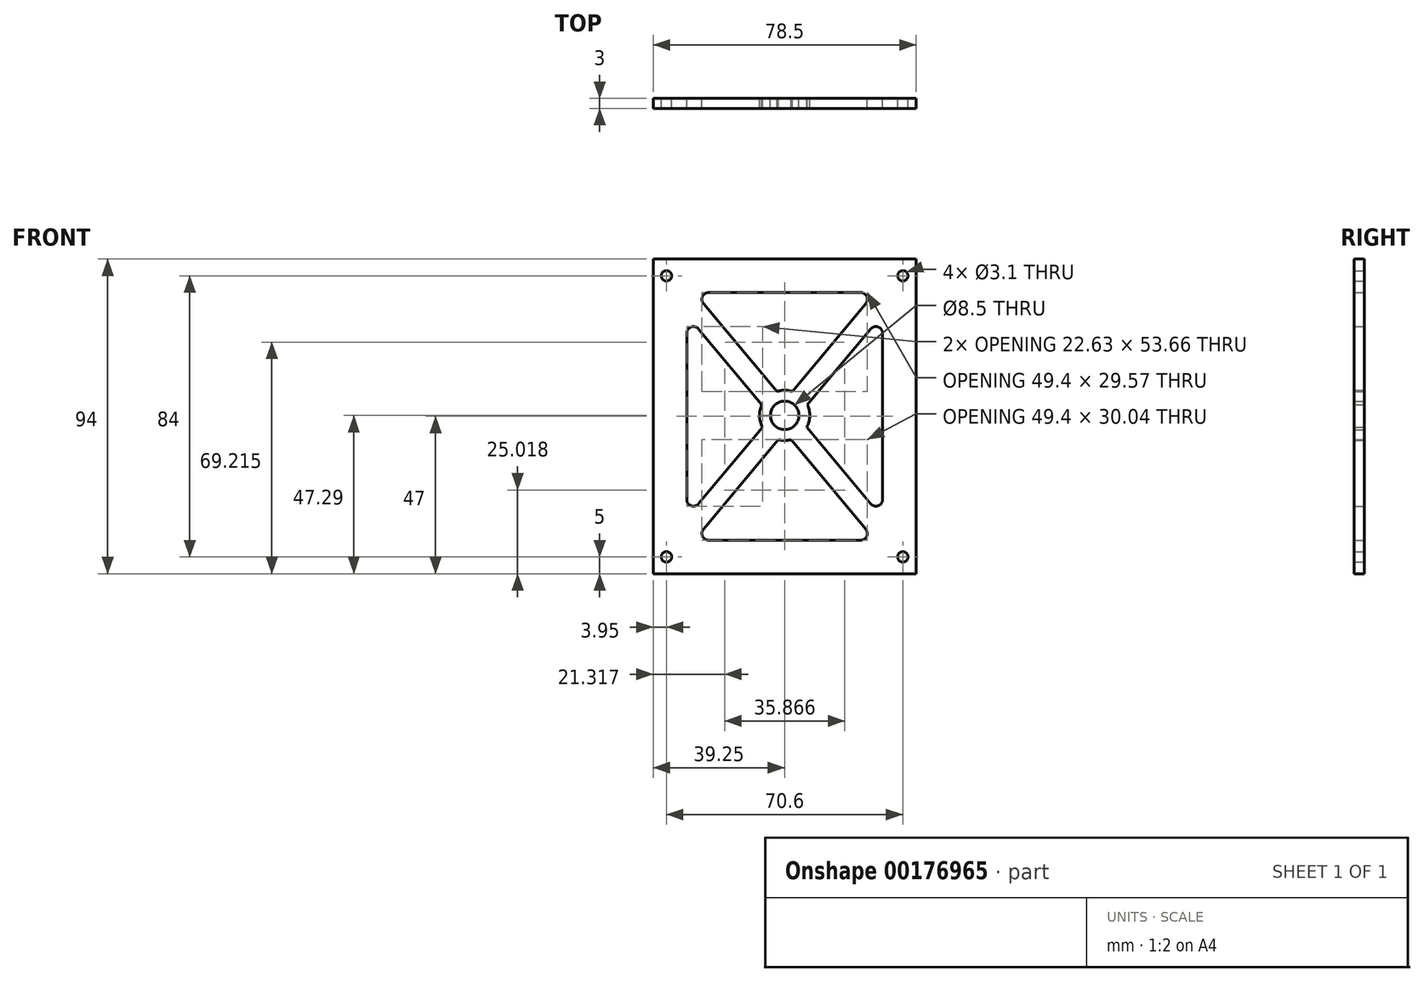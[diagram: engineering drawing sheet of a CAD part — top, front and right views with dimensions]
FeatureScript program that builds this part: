
annotation { "Feature Type Name" : "Feature", "Feature Type Description" : "" }
export const myFeature = defineFeature(function(context is Context, id is Id, definition is map)
    precondition{}
    {
        {
            var Q0;
            Q0=qCreatedBy(makeId("Front.planeOp"),FACE);
            var sketch = newSketch(context, id + "F0", { "sketchPlane" : qUnion([Q0])});
            skLineSegment(sketch, "E0.bottom", {"start": v(-39.25, 46.71) * mm, "end": v(39.25, 46.71) * mm});
            skLineSegment(sketch, "E0.top", {"start": v(-39.25, -47.29) * mm, "end": v(39.25, -47.29) * mm});
            skLineSegment(sketch, "E0.left", {"start": v(-39.25, 46.71) * mm, "end": v(-39.25, -47.29) * mm});
            skLineSegment(sketch, "E0.right", {"start": v(39.25, 46.71) * mm, "end": v(39.25, -47.29) * mm});
            skCircle(sketch, "E1", {"center": v(35.3, 41.71) * mm, "radius": 1.55 * mm});
            skCircle(sketch, "E2.MirrorC", {"center": v(-35.3, 41.71) * mm, "radius": 1.55 * mm});
            skCircle(sketch, "E3.MirrorC", {"center": v(-35.3, -42.29) * mm, "radius": 1.55 * mm});
            skCircle(sketch, "E4.MirrorC", {"center": v(35.3, -42.29) * mm, "radius": 1.55 * mm});
            skCircle(sketch, "E5", {"center": v(0, 0) * mm, "radius": 4.25 * mm});
            skArc(sketch, "E6", {"start": v(-1.9, -7.25) * mm, "mid": v(0, -7.5) * mm, "end": v(1.9, -7.25) * mm});
            skLineSegment(sketch, "E7", {"start": v(-39.25, -47.29) * mm, "end": v(39.25, 46.71) * mm, "construction": true});
            skLineSegment(sketch, "E8.0", {"start": v(-29.25, 24.54) * mm, "end": v(-29.25, -25.12) * mm});
            skLineSegment(sketch, "E8.1", {"start": v(-22.71, 36.71) * mm, "end": v(22.71, 36.71) * mm});
            skLineSegment(sketch, "E8.3", {"start": v(-22.71, -37.29) * mm, "end": v(22.71, -37.29) * mm});
            skArc(sketch, "E9.trimOffspring", {"start": v(2.3, 7.14) * mm, "mid": v(0, 7.5) * mm, "end": v(-2.3, 7.14) * mm});
            skLineSegment(sketch, "E10.trimOffspring", {"start": v(6.8, 3.17) * mm, "end": v(25.71, 25.82) * mm});
            skLineSegment(sketch, "E11.trimOffspring", {"start": v(2.3, 7.14) * mm, "end": v(24.25, 33.43) * mm});
            skLineSegment(sketch, "E12.trimOffspring", {"start": v(-24.25, -34) * mm, "end": v(-1.9, -7.25) * mm});
            skLineSegment(sketch, "E13.trimOffspring", {"start": v(-25.71, -26.4) * mm, "end": v(-6.62, -3.53) * mm});
            skLineSegment(sketch, "E14.trimOffspring", {"start": v(29.25, 24.54) * mm, "end": v(29.25, -25.12) * mm});
            skLineSegment(sketch, "E15.MirrorCS", {"start": v(24.25, -34) * mm, "end": v(1.9, -7.25) * mm});
            skLineSegment(sketch, "E16.MirrorCS", {"start": v(25.71, -26.4) * mm, "end": v(6.62, -3.53) * mm});
            skLineSegment(sketch, "E17.MirrorCS", {"start": v(-6.8, 3.17) * mm, "end": v(-25.71, 25.82) * mm});
            skLineSegment(sketch, "E18.MirrorCS", {"start": v(-2.3, 7.14) * mm, "end": v(-24.25, 33.43) * mm});
            skArc(sketch, "E19.trimOffspring", {"start": v(6.62, -3.53) * mm, "mid": v(7.5, -0.2) * mm, "end": v(6.8, 3.17) * mm});
            skArc(sketch, "E20.trimOffspring", {"start": v(-6.8, 3.17) * mm, "mid": v(-7.5, -0.2) * mm, "end": v(-6.62, -3.53) * mm});
            skPoint(sketch, "E21.visualSharp", {"position": v(-29.25, 30.06) * mm});
            skArc(sketch, "E21.filletArc", {"start": v(-25.71, 25.82) * mm, "mid": v(-27.93, 26.42) * mm, "end": v(-29.25, 24.54) * mm});
            skPoint(sketch, "E22.visualSharp", {"position": v(-27, 36.71) * mm});
            skArc(sketch, "E22.filletArc", {"start": v(-22.71, 36.71) * mm, "mid": v(-24.53, 35.56) * mm, "end": v(-24.25, 33.43) * mm});
            skPoint(sketch, "E23.visualSharp", {"position": v(27, 36.71) * mm});
            skArc(sketch, "E23.filletArc", {"start": v(24.25, 33.43) * mm, "mid": v(24.53, 35.56) * mm, "end": v(22.71, 36.71) * mm});
            skPoint(sketch, "E24.visualSharp", {"position": v(29.25, 30.06) * mm});
            skArc(sketch, "E24.filletArc", {"start": v(29.25, 24.54) * mm, "mid": v(27.93, 26.42) * mm, "end": v(25.71, 25.82) * mm});
            skPoint(sketch, "E25.visualSharp", {"position": v(29.25, -30.63) * mm});
            skArc(sketch, "E25.filletArc", {"start": v(25.71, -26.4) * mm, "mid": v(27.93, -27) * mm, "end": v(29.25, -25.12) * mm});
            skPoint(sketch, "E26.visualSharp", {"position": v(27, -37.29) * mm});
            skArc(sketch, "E26.filletArc", {"start": v(22.71, -37.29) * mm, "mid": v(24.53, -36.14) * mm, "end": v(24.25, -34) * mm});
            skPoint(sketch, "E27.visualSharp", {"position": v(-27, -37.29) * mm});
            skArc(sketch, "E27.filletArc", {"start": v(-24.25, -34) * mm, "mid": v(-24.53, -36.14) * mm, "end": v(-22.71, -37.29) * mm});
            skPoint(sketch, "E28.visualSharp", {"position": v(-29.25, -30.63) * mm});
            skArc(sketch, "E28.filletArc", {"start": v(-29.25, -25.12) * mm, "mid": v(-27.93, -27) * mm, "end": v(-25.71, -26.4) * mm});
            skSolve(sketch);
        }
        {
            var Q0;
            Q0=makeQuery(id+"F0.imprint","IMPRINT",FACE,{"disambiguationData":[TD([[makeQuery(id+"F0.imprint","IMPRINT",EDGE,{"derivedFrom":sQuery(id+"F0.wireOp",EDGE,"E0.bottom")}),-1.0]])]});
            extrude(context, id + "F1", {"entities" : qUnion([Q0]), "depth" : 3 * mm});
        }
    });
